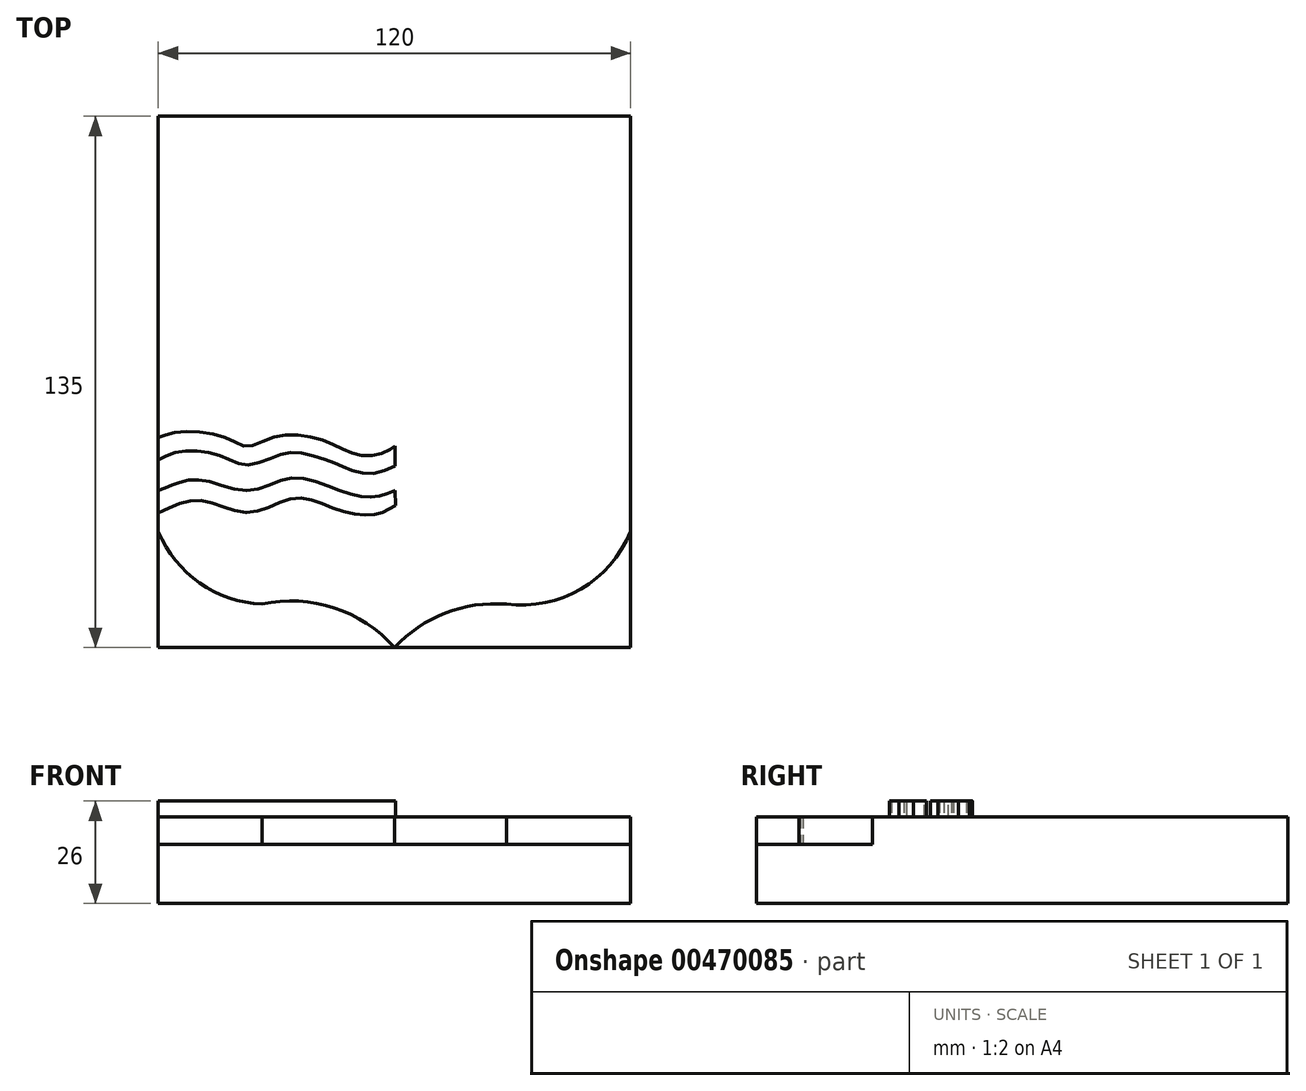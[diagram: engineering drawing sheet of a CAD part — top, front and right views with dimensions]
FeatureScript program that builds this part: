
annotation { "Feature Type Name" : "Feature", "Feature Type Description" : "" }
export const myFeature = defineFeature(function(context is Context, id is Id, definition is map)
    precondition{}
    {
        {
            var Q0;
            Q0=qCreatedBy(makeId("Top.planeOp"),FACE);
            var sketch = newSketch(context, id + "F0", { "sketchPlane" : qUnion([Q0])});
            skLineSegment(sketch, "E0.bottom", {"start": v(-60, 67.5) * mm, "end": v(60, 67.5) * mm});
            skLineSegment(sketch, "E0.top", {"start": v(-60, -67.5) * mm, "end": v(60, -67.5) * mm});
            skLineSegment(sketch, "E0.left", {"start": v(-60, 67.5) * mm, "end": v(-60, -67.5) * mm});
            skLineSegment(sketch, "E0.right", {"start": v(60, 67.5) * mm, "end": v(60, -67.5) * mm});
            skLineSegment(sketch, "E1", {"start": v(0, 67.5) * mm, "end": v(0, -67.5) * mm});
            skLineSegment(sketch, "E2", {"start": v(-60, 0) * mm, "end": v(60, 0) * mm});
            skLineSegment(sketch, "E3", {"start": v(5.98, 0) * mm, "end": v(29.66, 16.67) * mm});
            skSolve(sketch);
        }
        {
            var Q0;
            Q0=qSketchRegion(id+"F0",true);
            extrude(context, id + "F1", {"entities" : qUnion([Q0]), "depth" : 15 * mm});
        }
        {
            var Q0;
            Q0=makeQuery(id+"F1.opExtrude","CAP_FACE",FACE,{"disambiguationData":[OSD([sQuery(id+"F0.wireOp",EDGE,"E0.bottom"),sQuery(id+"F0.wireOp",EDGE,"E0.top"),sQuery(id+"F0.wireOp",EDGE,"E0.left"),sQuery(id+"F0.wireOp",EDGE,"E0.right")])],"isStart":false});
            var sketch = newSketch(context, id + "F2", { "sketchPlane" : qUnion([Q0])});
            skLineSegment(sketch, "E4", {"start": v(30.81, 17.82) * mm, "end": v(9.66, 0) * mm});
            skLineSegment(sketch, "E5", {"start": v(30.81, 17.82) * mm, "end": v(50.12, 0) * mm});
            skLineSegment(sketch, "E6", {"start": v(30.81, 25.64) * mm, "end": v(58.6, 0) * mm});
            skLineSegment(sketch, "E7", {"start": v(30.81, 25.64) * mm, "end": v(0.38, 0) * mm});
            skLineSegment(sketch, "E8", {"start": v(0, 0) * mm, "end": v(60, 0) * mm});
            skLineSegment(sketch, "E9", {"start": v(0.38, 67.5) * mm, "end": v(0.38, 0) * mm});
            skLineSegment(sketch, "E10", {"start": v(30.81, 35.52) * mm, "end": v(0, 9.57) * mm});
            skLineSegment(sketch, "E11", {"start": v(30.81, 35.52) * mm, "end": v(60, 9.57) * mm});
            skLineSegment(sketch, "E12", {"start": v(0.38, 20.35) * mm, "end": v(30.81, 45.99) * mm});
            skLineSegment(sketch, "E13", {"start": v(30.81, 45.99) * mm, "end": v(60, 18.97) * mm});
            skLineSegment(sketch, "E14", {"start": v(0.38, 31.84) * mm, "end": v(30.81, 57.48) * mm});
            skLineSegment(sketch, "E15", {"start": v(30.81, 57.48) * mm, "end": v(60, 31.16) * mm});
            skLineSegment(sketch, "E16", {"start": v(0.38, 43.57) * mm, "end": v(30.81, 67.5) * mm});
            skLineSegment(sketch, "E17", {"start": v(30.81, 67.5) * mm, "end": v(60, 41.17) * mm});
            skSolve(sketch);
        }
        {
            var Q0;
            {var subQ0=sQuery(id+"F2.wireOp",EDGE,"E16");var subQ1=sQuery(id+"F2.wireOp",EDGE,"E14");var subQ2=sQuery(id+"F2.wireOp",EDGE,"E13");var subQ3=sQuery(id+"F2.wireOp",EDGE,"E12");var subQ4=sQuery(id+"F2.wireOp",EDGE,"E11");var subQ5=sQuery(id+"F2.wireOp",EDGE,"E10");var subQ6=sQuery(id+"F2.wireOp",EDGE,"E9");var subQ7=sQuery(id+"F2.wireOp",EDGE,"E8");var subQ8=sQuery(id+"F2.wireOp",EDGE,"E5");var subQ9=sQuery(id+"F2.wireOp",EDGE,"E6");var subQ10=sQuery(id+"F0.wireOp",EDGE,"E0.right");var subQ11=makeQuery(id+"F1.opExtrude","CAP_EDGE",EDGE,{"disambiguationData":[OSD([subQ10])],"isStart":false});var subQ12=sQuery(id+"F0.wireOp",EDGE,"E0.top");var subQ13=sQuery(id+"F2.wireOp",EDGE,"E17");var subQ14=sQuery(id+"F0.wireOp",EDGE,"E0.left");var subQ15=sQuery(id+"F0.wireOp",EDGE,"E0.bottom");var subQ16=makeQuery(id+"F1.opExtrude","CAP_FACE",FACE,{"disambiguationData":[OSD([subQ15,subQ12,subQ14,subQ10])],"isStart":false});var subQ17=sQuery(id+"F2.wireOp",EDGE,"E15");var subQ18=sQuery(id+"F2.wireOp",EDGE,"E4");var subQ19=sQuery(id+"F2.wireOp",EDGE,"E7");Q0=makeQuery(id+"FIwiPj0ks3UmRnG_1.boolean.opBoolean","SPLIT",FACE,{"disambiguationData":[TD([makeQuery(id+"F1.opExtrude","SWEPT_FACE",FACE,{"disambiguationData":[OSD([subQ15])]}),subQ16,makeQuery(id+"F1.opExtrude","SWEPT_FACE",FACE,{"disambiguationData":[OSD([subQ12])]}),makeQuery(id+"F1.opExtrude","SWEPT_FACE",FACE,{"disambiguationData":[OSD([subQ14])]}),makeQuery(id+"F1.opExtrude","SWEPT_FACE",FACE,{"disambiguationData":[OSD([subQ10])]}),makeQuery(id+"FIwiPj0ks3UmRnG_1.opExtrude","SWEPT_FACE",FACE,{"disambiguationData":[OSD([subQ18])]}),makeQuery(id+"FIwiPj0ks3UmRnG_1.opExtrude","SWEPT_FACE",FACE,{"disambiguationData":[OSD([subQ8])]}),makeQuery(id+"FIwiPj0ks3UmRnG_1.opExtrude","SWEPT_FACE",FACE,{"disambiguationData":[OSD([subQ9])]}),makeQuery(id+"FIwiPj0ks3UmRnG_1.opExtrude","SWEPT_FACE",FACE,{"disambiguationData":[OSD([subQ19])]}),makeQuery(id+"FIwiPj0ks3UmRnG_1.opExtrude","SWEPT_FACE",FACE,{"disambiguationData":[OSD([subQ7]),TDD([makeQuery(id+"F2.imprint","IMPRINT",EDGE,{"disambiguationData":[TD([[makeQuery(id+"F2.imprint","INTERSECT",VERTEX,{"derivedFrom":[subQ18,subQ7]}),1.0]])],"derivedFrom":subQ7})])]}),makeQuery(id+"FIwiPj0ks3UmRnG_1.opExtrude","SWEPT_FACE",FACE,{"disambiguationData":[OSD([subQ7]),TDD([makeQuery(id+"F2.imprint","IMPRINT",EDGE,{"disambiguationData":[TD([[makeQuery(id+"F2.imprint","INTERSECT",VERTEX,{"derivedFrom":[subQ8,subQ7]}),-1.0]])],"derivedFrom":subQ7})])]}),makeQuery(id+"FIwiPj0ks3UmRnG_1.opExtrude","SWEPT_FACE",FACE,{"disambiguationData":[OSD([subQ6]),TDD([makeQuery(id+"F2.imprint","IMPRINT",EDGE,{"disambiguationData":[TD([[makeQuery(id+"F2.imprint","INTERSECT",VERTEX,{"derivedFrom":[subQ6,subQ1]}),1.0]])],"derivedFrom":subQ6})])]}),makeQuery(id+"FIwiPj0ks3UmRnG_1.opExtrude","SWEPT_FACE",FACE,{"disambiguationData":[OSD([subQ6]),TDD([makeQuery(id+"F2.imprint","IMPRINT",EDGE,{"disambiguationData":[TD([[makeQuery(id+"F2.imprint","INTERSECT",VERTEX,{"derivedFrom":[subQ6,subQ3]}),-1.0]])],"derivedFrom":subQ6})])]}),makeQuery(id+"FIwiPj0ks3UmRnG_1.opExtrude","SWEPT_FACE",FACE,{"disambiguationData":[OSD([subQ5])]}),makeQuery(id+"FIwiPj0ks3UmRnG_1.opExtrude","SWEPT_FACE",FACE,{"disambiguationData":[OSD([subQ4])]}),makeQuery(id+"FIwiPj0ks3UmRnG_1.opExtrude","SWEPT_FACE",FACE,{"disambiguationData":[OSD([subQ3])]}),makeQuery(id+"FIwiPj0ks3UmRnG_1.opExtrude","SWEPT_FACE",FACE,{"disambiguationData":[OSD([subQ2])]}),makeQuery(id+"FIwiPj0ks3UmRnG_1.opExtrude","SWEPT_FACE",FACE,{"disambiguationData":[OSD([subQ1])]}),makeQuery(id+"FIwiPj0ks3UmRnG_1.opExtrude","SWEPT_FACE",FACE,{"disambiguationData":[OSD([subQ17])]}),makeQuery(id+"FIwiPj0ks3UmRnG_1.opExtrude","SWEPT_FACE",FACE,{"disambiguationData":[OSD([subQ0])]}),makeQuery(id+"FIwiPj0ks3UmRnG_1.opExtrude","SWEPT_FACE",FACE,{"disambiguationData":[OSD([subQ13])]}),makeQuery(id+"FIwiPj0ks3UmRnG_1.opExtrude","SWEPT_FACE",FACE,{"disambiguationData":[OSD([subQ10]),TDD([makeQuery(id+"F2.imprint","IMPRINT",EDGE,{"disambiguationData":[TD([[makeQuery(id+"F2.imprint","INTERSECT",VERTEX,{"derivedFrom":[subQ11,subQ4]}),1.0]])],"derivedFrom":subQ11})])]}),makeQuery(id+"FIwiPj0ks3UmRnG_1.opExtrude","SWEPT_FACE",FACE,{"disambiguationData":[OSD([subQ10]),TDD([makeQuery(id+"F2.imprint","IMPRINT",EDGE,{"disambiguationData":[TD([[makeQuery(id+"F2.imprint","INTERSECT",VERTEX,{"derivedFrom":[subQ11,subQ17]}),1.0]])],"derivedFrom":subQ11})])]})])],"derivedFrom":subQ16});}
            var sketch = newSketch(context, id + "F3", { "sketchPlane" : qUnion([Q0])});
            skLineSegment(sketch, "E18", {"start": v(-60, 0) * mm, "end": v(0, 0) * mm});
            skLineSegment(sketch, "E19", {"start": v(0, 0) * mm, "end": v(0, 67.5) * mm});
            skLineSegment(sketch, "E20", {"start": v(-44.92, 3.85) * mm, "end": v(-44.92, 43.85) * mm});
            skLineSegment(sketch, "E21", {"start": v(-14.68, 3.85) * mm, "end": v(-14.68, 43.85) * mm});
            skLineSegment(sketch, "E22", {"start": v(-44.92, 43.85) * mm, "end": v(-29.05, 61.11) * mm});
            skLineSegment(sketch, "E23", {"start": v(-29.05, 61.11) * mm, "end": v(-14.68, 43.85) * mm});
            skArc(sketch, "E24", {"start": v(-44.92, 43.85) * mm, "mid": v(-29.8, 42.25) * mm, "end": v(-14.68, 43.85) * mm});
            skArc(sketch, "E25", {"start": v(-44.92, 3.85) * mm, "mid": v(-29.8, 2.25) * mm, "end": v(-14.68, 3.85) * mm});
            skLineSegment(sketch, "E26", {"start": v(-34.44, 2.4) * mm, "end": v(-34.44, 12.95) * mm});
            skLineSegment(sketch, "E27", {"start": v(-26.52, 2.32) * mm, "end": v(-26.52, 12.95) * mm});
            skArc(sketch, "E28", {"start": v(-26.52, 12.95) * mm, "mid": v(-30.48, 16.9) * mm, "end": v(-34.44, 12.95) * mm});
            skLineSegment(sketch, "E29", {"start": v(-34.44, 2.4) * mm, "end": v(-31.8, 4.1) * mm});
            skLineSegment(sketch, "E30", {"start": v(-31.8, 4.1) * mm, "end": v(-31.8, 14.44) * mm});
            skArc(sketch, "E31", {"start": v(-30.48, 16.9) * mm, "mid": v(-31.46, 15.84) * mm, "end": v(-31.8, 14.44) * mm});
            skArc(sketch, "E32", {"start": v(-31.8, 4.1) * mm, "mid": v(-29.17, 3.86) * mm, "end": v(-26.52, 4.1) * mm});
            skLineSegment(sketch, "E33", {"start": v(-42.27, 38.01) * mm, "end": v(-42.27, 30.65) * mm});
            skLineSegment(sketch, "E34", {"start": v(-37.56, 30.2) * mm, "end": v(-37.56, 37.2) * mm});
            skArc(sketch, "E35", {"start": v(-42.27, 38.01) * mm, "mid": v(-39.98, 37.24) * mm, "end": v(-37.56, 37.2) * mm});
            skArc(sketch, "E36", {"start": v(-42.27, 30.65) * mm, "mid": v(-39.98, 29.73) * mm, "end": v(-37.56, 30.2) * mm});
            skLineSegment(sketch, "E37", {"start": v(-42.27, 30.65) * mm, "end": v(-40.62, 31.44) * mm});
            skLineSegment(sketch, "E38", {"start": v(-40.62, 31.44) * mm, "end": v(-40.62, 37.38) * mm});
            skArc(sketch, "E39", {"start": v(-40.62, 31.44) * mm, "mid": v(-39.1, 31.14) * mm, "end": v(-37.56, 31.44) * mm});
            skLineSegment(sketch, "E40", {"start": v(-31.97, 37.24) * mm, "end": v(-31.97, 29.9) * mm});
            skLineSegment(sketch, "E41", {"start": v(-26.6, 37.24) * mm, "end": v(-26.6, 29.9) * mm});
            skArc(sketch, "E42", {"start": v(-31.97, 29.9) * mm, "mid": v(-29.28, 29.34) * mm, "end": v(-26.6, 29.9) * mm});
            skArc(sketch, "E43", {"start": v(-31.97, 37.24) * mm, "mid": v(-29.28, 36.81) * mm, "end": v(-26.6, 37.24) * mm});
            skLineSegment(sketch, "E44", {"start": v(-31.97, 29.9) * mm, "end": v(-31.1, 30.76) * mm});
            skLineSegment(sketch, "E45", {"start": v(-31.1, 30.76) * mm, "end": v(-31.1, 37) * mm});
            skArc(sketch, "E46", {"start": v(-31.1, 30.76) * mm, "mid": v(-28.84, 30.28) * mm, "end": v(-26.6, 30.76) * mm});
            skLineSegment(sketch, "E47", {"start": v(-16.58, 38.06) * mm, "end": v(-16.58, 30.66) * mm});
            skLineSegment(sketch, "E48", {"start": v(-21.32, 37.33) * mm, "end": v(-21.32, 29.89) * mm});
            skArc(sketch, "E49", {"start": v(-21.32, 37.33) * mm, "mid": v(-18.88, 37.24) * mm, "end": v(-16.58, 38.06) * mm});
            skArc(sketch, "E50", {"start": v(-21.32, 29.89) * mm, "mid": v(-18.85, 29.65) * mm, "end": v(-16.58, 30.66) * mm});
            skLineSegment(sketch, "E51", {"start": v(-16.58, 30.66) * mm, "end": v(-17.93, 31.14) * mm});
            skLineSegment(sketch, "E52", {"start": v(-17.93, 31.14) * mm, "end": v(-17.93, 37.46) * mm});
            skSolve(sketch);
        }
        {
            var Q0;
            {var subQ0=sQuery(id+"F2.wireOp",EDGE,"E16");var subQ1=makeQuery(id+"FIwiPj0ks3UmRnG_1.opExtrude","SWEPT_FACE",FACE,{"disambiguationData":[OSD([subQ0])]});var subQ2=sQuery(id+"F2.wireOp",EDGE,"E14");var subQ3=makeQuery(id+"FIwiPj0ks3UmRnG_1.opExtrude","SWEPT_FACE",FACE,{"disambiguationData":[OSD([subQ2])]});var subQ4=sQuery(id+"F2.wireOp",EDGE,"E13");var subQ5=makeQuery(id+"FIwiPj0ks3UmRnG_1.opExtrude","SWEPT_FACE",FACE,{"disambiguationData":[OSD([subQ4])]});var subQ6=sQuery(id+"F2.wireOp",EDGE,"E12");var subQ7=makeQuery(id+"FIwiPj0ks3UmRnG_1.opExtrude","SWEPT_FACE",FACE,{"disambiguationData":[OSD([subQ6])]});var subQ8=sQuery(id+"F2.wireOp",EDGE,"E11");var subQ9=makeQuery(id+"FIwiPj0ks3UmRnG_1.opExtrude","SWEPT_FACE",FACE,{"disambiguationData":[OSD([subQ8])]});var subQ11=sQuery(id+"F2.wireOp",EDGE,"E10");var subQ12=makeQuery(id+"FIwiPj0ks3UmRnG_1.opExtrude","SWEPT_FACE",FACE,{"disambiguationData":[OSD([subQ11])]});var subQ14=sQuery(id+"F2.wireOp",EDGE,"E9");var subQ15=makeQuery(id+"FIwiPj0ks3UmRnG_1.opExtrude","SWEPT_FACE",FACE,{"disambiguationData":[OSD([subQ14]),TDD([makeQuery(id+"F2.imprint","IMPRINT",EDGE,{"disambiguationData":[TD([[makeQuery(id+"F2.imprint","INTERSECT",VERTEX,{"derivedFrom":[subQ14,subQ6]}),-1.0]])],"derivedFrom":subQ14})])]});var subQ16=makeQuery(id+"FIwiPj0ks3UmRnG_1.opExtrude","SWEPT_FACE",FACE,{"disambiguationData":[OSD([subQ14]),TDD([makeQuery(id+"F2.imprint","IMPRINT",EDGE,{"disambiguationData":[TD([[makeQuery(id+"F2.imprint","INTERSECT",VERTEX,{"derivedFrom":[subQ14,subQ2]}),1.0]])],"derivedFrom":subQ14})])]});var subQ17=sQuery(id+"F2.wireOp",EDGE,"E8");var subQ18=sQuery(id+"F2.wireOp",EDGE,"E5");var subQ19=sQuery(id+"F2.wireOp",EDGE,"E6");var subQ20=makeQuery(id+"FIwiPj0ks3UmRnG_1.opExtrude","SWEPT_FACE",FACE,{"disambiguationData":[OSD([subQ17]),TDD([makeQuery(id+"F2.imprint","IMPRINT",EDGE,{"disambiguationData":[TD([[makeQuery(id+"F2.imprint","INTERSECT",VERTEX,{"derivedFrom":[subQ18,subQ17]}),-1.0]])],"derivedFrom":subQ17})])]});var subQ21=makeQuery(id+"FIwiPj0ks3UmRnG_1.opExtrude","SWEPT_FACE",FACE,{"disambiguationData":[OSD([subQ18])]});var subQ22=sQuery(id+"F0.wireOp",EDGE,"E0.right");var subQ23=makeQuery(id+"F1.opExtrude","CAP_EDGE",EDGE,{"disambiguationData":[OSD([subQ22])],"isStart":false});var subQ24=makeQuery(id+"FIwiPj0ks3UmRnG_1.opExtrude","SWEPT_FACE",FACE,{"disambiguationData":[OSD([subQ22]),TDD([makeQuery(id+"F2.imprint","IMPRINT",EDGE,{"disambiguationData":[TD([[makeQuery(id+"F2.imprint","INTERSECT",VERTEX,{"derivedFrom":[subQ23,subQ8]}),1.0]])],"derivedFrom":subQ23})])]});var subQ25=sQuery(id+"F0.wireOp",EDGE,"E0.top");var subQ26=makeQuery(id+"F1.opExtrude","SWEPT_FACE",FACE,{"disambiguationData":[OSD([subQ25])]});var subQ27=sQuery(id+"F2.wireOp",EDGE,"E17");var subQ28=makeQuery(id+"FIwiPj0ks3UmRnG_1.opExtrude","SWEPT_FACE",FACE,{"disambiguationData":[OSD([subQ27])]});var subQ29=sQuery(id+"F0.wireOp",EDGE,"E0.left");var subQ30=sQuery(id+"F0.wireOp",EDGE,"E0.bottom");var subQ31=makeQuery(id+"F1.opExtrude","CAP_FACE",FACE,{"disambiguationData":[OSD([subQ30,subQ25,subQ29,subQ22])],"isStart":false});var subQ32=sQuery(id+"F2.wireOp",EDGE,"E15");var subQ33=makeQuery(id+"FIwiPj0ks3UmRnG_1.opExtrude","SWEPT_FACE",FACE,{"disambiguationData":[OSD([subQ32])]});var subQ34=makeQuery(id+"F1.opExtrude","SWEPT_FACE",FACE,{"disambiguationData":[OSD([subQ30])]});var subQ35=makeQuery(id+"F1.opExtrude","SWEPT_FACE",FACE,{"disambiguationData":[OSD([subQ22])]});var subQ36=makeQuery(id+"FIwiPj0ks3UmRnG_1.opExtrude","SWEPT_FACE",FACE,{"disambiguationData":[OSD([subQ19])]});var subQ37=makeQuery(id+"F1.opExtrude","SWEPT_FACE",FACE,{"disambiguationData":[OSD([subQ29])]});var subQ38=makeQuery(id+"FIwiPj0ks3UmRnG_1.opExtrude","SWEPT_FACE",FACE,{"disambiguationData":[OSD([subQ22]),TDD([makeQuery(id+"F2.imprint","IMPRINT",EDGE,{"disambiguationData":[TD([[makeQuery(id+"F2.imprint","INTERSECT",VERTEX,{"derivedFrom":[subQ23,subQ32]}),1.0]])],"derivedFrom":subQ23})])]});var subQ39=sQuery(id+"F2.wireOp",EDGE,"E4");var subQ40=makeQuery(id+"FIwiPj0ks3UmRnG_1.opExtrude","SWEPT_FACE",FACE,{"disambiguationData":[OSD([subQ39])]});var subQ41=sQuery(id+"F2.wireOp",EDGE,"E7");var subQ42=makeQuery(id+"FIwiPj0ks3UmRnG_1.opExtrude","SWEPT_FACE",FACE,{"disambiguationData":[OSD([subQ41])]});var subQ43=makeQuery(id+"FIwiPj0ks3UmRnG_1.opExtrude","SWEPT_FACE",FACE,{"disambiguationData":[OSD([subQ17]),TDD([makeQuery(id+"F2.imprint","IMPRINT",EDGE,{"disambiguationData":[TD([[makeQuery(id+"F2.imprint","INTERSECT",VERTEX,{"derivedFrom":[subQ39,subQ17]}),1.0]])],"derivedFrom":subQ17})])]});Q0=makeQuery(id+"FrnWBSIW1grvK7o_1.boolean.opBoolean","SPLIT",FACE,{"disambiguationData":[TD([subQ34])],"derivedFrom":makeQuery(id+"FIwiPj0ks3UmRnG_1.boolean.opBoolean","SPLIT",FACE,{"disambiguationData":[TD([subQ34,subQ31,subQ26,subQ37,subQ35,subQ40,subQ21,subQ36,subQ42,subQ43,subQ20,subQ16,subQ15,subQ12,subQ9,subQ7,subQ5,subQ3,subQ33,subQ1,subQ28,subQ24,subQ38])],"derivedFrom":subQ31})});}
            var sketch = newSketch(context, id + "F4", { "sketchPlane" : qUnion([Q0])});
            skArc(sketch, "E53", {"start": v(-60, -38.05) * mm, "mid": v(-49.51, -51.1) * mm, "end": v(-33.67, -56.48) * mm});
            skArc(sketch, "E54", {"start": v(0, -67.5) * mm, "mid": v(-15.34, -57.42) * mm, "end": v(-33.67, -56.48) * mm});
            skArc(sketch, "E55", {"start": v(28.41, -56.48) * mm, "mid": v(47.34, -52.64) * mm, "end": v(60, -38.05) * mm});
            skArc(sketch, "E56", {"start": v(28.41, -56.48) * mm, "mid": v(12.94, -58.74) * mm, "end": v(0, -67.5) * mm});
            skLineSegment(sketch, "E57", {"start": v(-60, 0) * mm, "end": v(58.6, 0) * mm});
            skLineSegment(sketch, "E58", {"start": v(60, -67.5) * mm, "end": v(0, -67.5) * mm});
            skLineSegment(sketch, "E59", {"start": v(-60, -67.5) * mm, "end": v(-60, 0) * mm});
            skSolve(sketch);
        }
        {
            var Q0;
            {var subQ23=sQuery(id+"F4.wireOp",EDGE,"E53");Q0=makeQuery(id+"F4.imprint","IMPRINT",FACE,{"disambiguationData":[TD([[makeQuery(id+"F4.imprint","IMPRINT",EDGE,{"derivedFrom":subQ23}),1.0]])]});}
            extrude(context, id + "F5", {"entities" : qUnion([Q0]), "operationType" : NewBodyOperationType.ADD, "depth" : 7 * mm});
        }
        {
            var Q0;
            Q0=makeQuery(id+"F5.opExtrude","CAP_FACE",FACE,{"disambiguationData":[OSD([sQuery(id+"F0.wireOp",EDGE,"E0.bottom"),sQuery(id+"F0.wireOp",EDGE,"E0.left"),sQuery(id+"F0.wireOp",EDGE,"E0.right"),sQuery(id+"F2.wireOp",EDGE,"E6"),sQuery(id+"F2.wireOp",EDGE,"E7"),sQuery(id+"F2.wireOp",EDGE,"E9"),sQuery(id+"F2.wireOp",EDGE,"E10"),sQuery(id+"F2.wireOp",EDGE,"E11"),sQuery(id+"F2.wireOp",EDGE,"E12"),sQuery(id+"F2.wireOp",EDGE,"E13"),sQuery(id+"F2.wireOp",EDGE,"E14"),sQuery(id+"F2.wireOp",EDGE,"E15"),sQuery(id+"F2.wireOp",EDGE,"E16"),sQuery(id+"F3.wireOp",EDGE,"E20"),sQuery(id+"F3.wireOp",EDGE,"E21"),sQuery(id+"F3.wireOp",EDGE,"E22"),sQuery(id+"F3.wireOp",EDGE,"E23"),sQuery(id+"F3.wireOp",EDGE,"E25"),sQuery(id+"F3.wireOp",EDGE,"E26"),sQuery(id+"F3.wireOp",EDGE,"E27"),sQuery(id+"F3.wireOp",EDGE,"E28"),sQuery(id+"F4.wireOp",EDGE,"E53"),sQuery(id+"F4.wireOp",EDGE,"E54"),sQuery(id+"F4.wireOp",EDGE,"E55"),sQuery(id+"F4.wireOp",EDGE,"E56"),sQuery(id+"F4.wireOp",EDGE,"E57"),sQuery(id+"F4.wireOp",EDGE,"E59")])],"isStart":false});
            var sketch = newSketch(context, id + "F6", { "sketchPlane" : qUnion([Q0])});
            skLineSegment(sketch, "E60", {"start": v(-60, 0) * mm, "end": v(0, 0) * mm});
            skLineSegment(sketch, "E61", {"start": v(0, 0) * mm, "end": v(0.38, -54.84) * mm});
            skLineSegment(sketch, "E62", {"start": v(0.38, -54.84) * mm, "end": v(-60, -55.25) * mm});
            skLineSegment(sketch, "E63", {"start": v(-60, -55.25) * mm, "end": v(-60, 0) * mm});
            skFitSpline(sketch, "E64", {"points": [v(-60, -33.3) * mm, v(-48.98, -30.2) * mm, v(-36.9, -33.2) * mm, v(-25.2, -29.52) * mm, v(-14.37, -32.52) * mm, v(-4.6, -33.58) * mm, v(0.22, -31.36) * mm], "startDerivative": vector(61.64, 29.79) * mm, "endDerivative": vector(35.81, 22.86) * mm});
            skPoint(sketch, "E65.3.internal.snap0", {"position": v(-60, -27.63) * mm});
            skPoint(sketch, "E65.5.internal.snap0", {"position": v(-60, -27.63) * mm});
            skPoint(sketch, "E65.7.internal.snap0", {"position": v(-60, -27.63) * mm});
            skFitSpline(sketch, "E65", {"points": [v(-60, -27.63) * mm, v(-55.85, -25.95) * mm, v(-48.89, -24.98) * mm, v(-36.7, -27.63) * mm, v(-25.97, -24.4) * mm, v(-13.99, -27.63) * mm, v(-5.38, -29.23) * mm, v(0.19, -27.63) * mm], "startDerivative": vector(38.1, 16.45) * mm, "endDerivative": vector(45.3, 18.41) * mm});
            skFitSpline(sketch, "E66", {"points": [v(-60, -19.85) * mm, v(-55.85, -18.02) * mm, v(-49.08, -17.73) * mm, v(-42.5, -19.47) * mm, v(-37.38, -21.11) * mm, v(-30.42, -18.98) * mm, v(-24.72, -18.02) * mm, v(-17.08, -19.95) * mm, v(-12.63, -21.79) * mm, v(-6.54, -23.34) * mm, v(0.15, -21.4) * mm], "startDerivative": vector(44.68, 24.94) * mm, "endDerivative": vector(62.72, 27.14) * mm});
            skFitSpline(sketch, "E67", {"points": [v(-60, -14.15) * mm, v(-56.72, -13.09) * mm, v(-49.18, -12.8) * mm, v(-41.44, -14.83) * mm, v(-37.28, -16.37) * mm, v(-31.68, -14.34) * mm, v(-24.33, -13.47) * mm, v(-16.8, -15.4) * mm, v(-11.67, -17.73) * mm, v(-6.64, -18.8) * mm, v(-1.8, -17.63) * mm, v(0.11, -16.28) * mm, v(0.11, -16.08) * mm], "startDerivative": vector(41.27, 16.7) * mm, "endDerivative": vector(-3.5, 10.12) * mm});
            skSolve(sketch);
        }
        {
            var Q0;
            {var subQ0=sQuery(id+"F6.wireOp",EDGE,"E66");Q0=makeQuery(id+"F6.imprint","IMPRINT",FACE,{"disambiguationData":[TD([[makeQuery(id+"F6.imprint","IMPRINT",EDGE,{"derivedFrom":subQ0}),1.0]])]});}
            var Q1;
            {var subQ0=sQuery(id+"F6.wireOp",EDGE,"E64");Q1=makeQuery(id+"F6.imprint","IMPRINT",FACE,{"disambiguationData":[TD([[makeQuery(id+"F6.imprint","IMPRINT",EDGE,{"derivedFrom":subQ0}),1.0]])]});}
            extrude(context, id + "F7", {"entities" : qUnion([Q0, Q1]), "operationType" : NewBodyOperationType.ADD, "depth" : 4 * mm});
        }
    });
